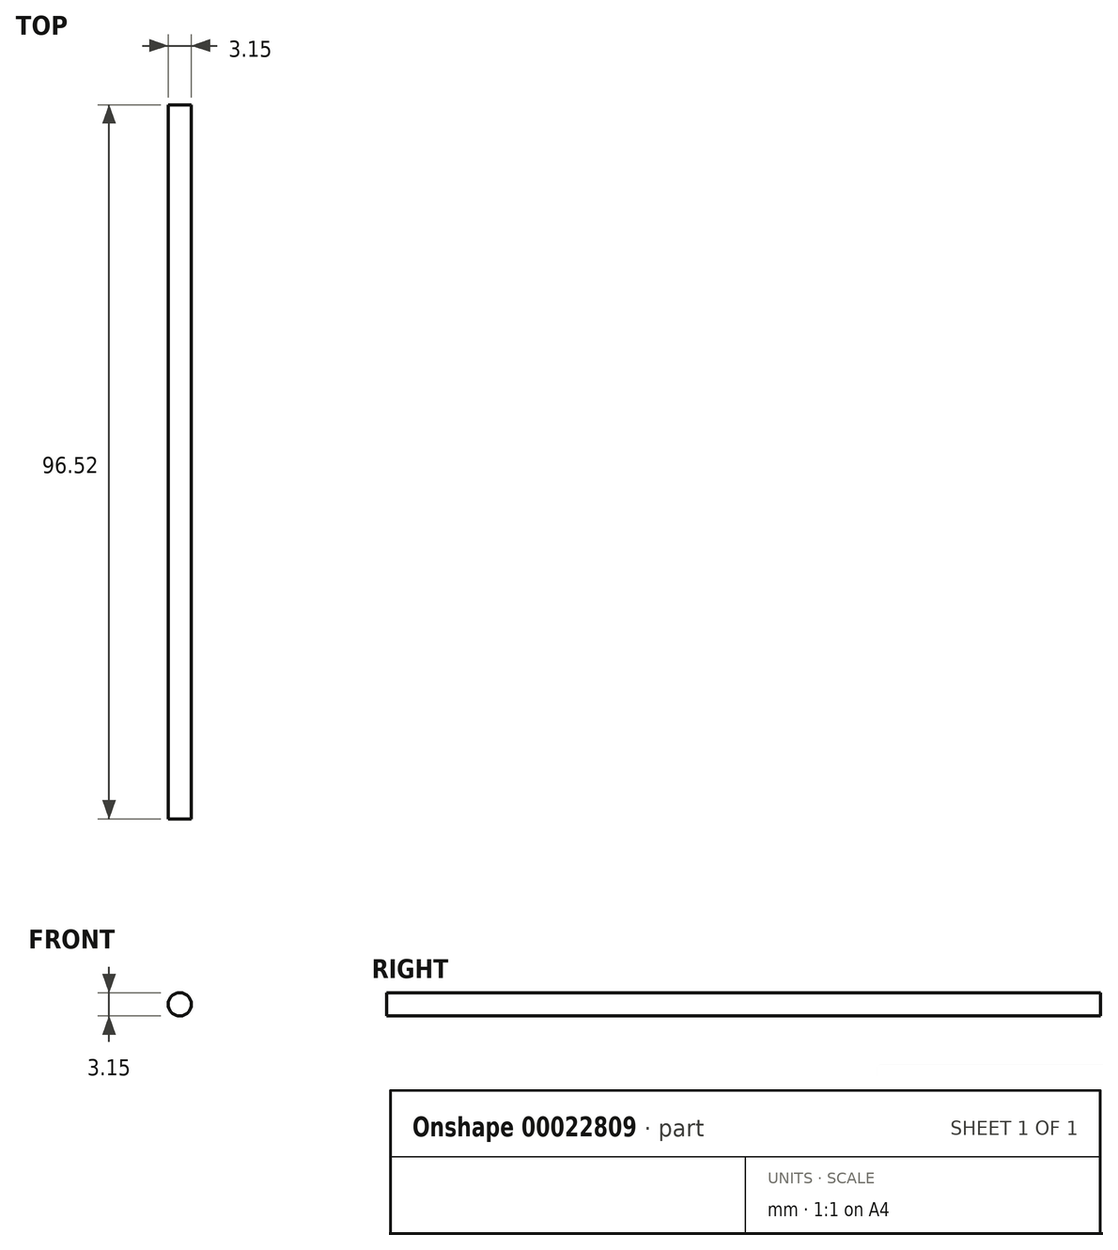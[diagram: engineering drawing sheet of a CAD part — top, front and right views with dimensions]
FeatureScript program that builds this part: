
annotation { "Feature Type Name" : "Feature", "Feature Type Description" : "" }
export const myFeature = defineFeature(function(context is Context, id is Id, definition is map)
    precondition{}
    {
        {
            var Q0;
            Q0=qCreatedBy(makeId("Front.planeOp"),FACE);
            var sketch = newSketch(context, id + "F0", { "sketchPlane" : qUnion([Q0])});
            skCircle(sketch, "E0", {"center": v(-58.64, 18.25) * mm, "radius": 1.57 * mm});
            skSolve(sketch);
        }
        {
            var Q0;
            Q0=makeQuery(id+"F0.imprint","IMPRINT",FACE,{"disambiguationData":[TD([[makeQuery(id+"F0.imprint","IMPRINT",EDGE,{"derivedFrom":sQuery(id+"F0.wireOp",EDGE,"E0")}),1.0]])]});
            extrude(context, id + "F1", {"entities" : qUnion([Q0]), "depth" : 96.52 * mm});
        }
    });
